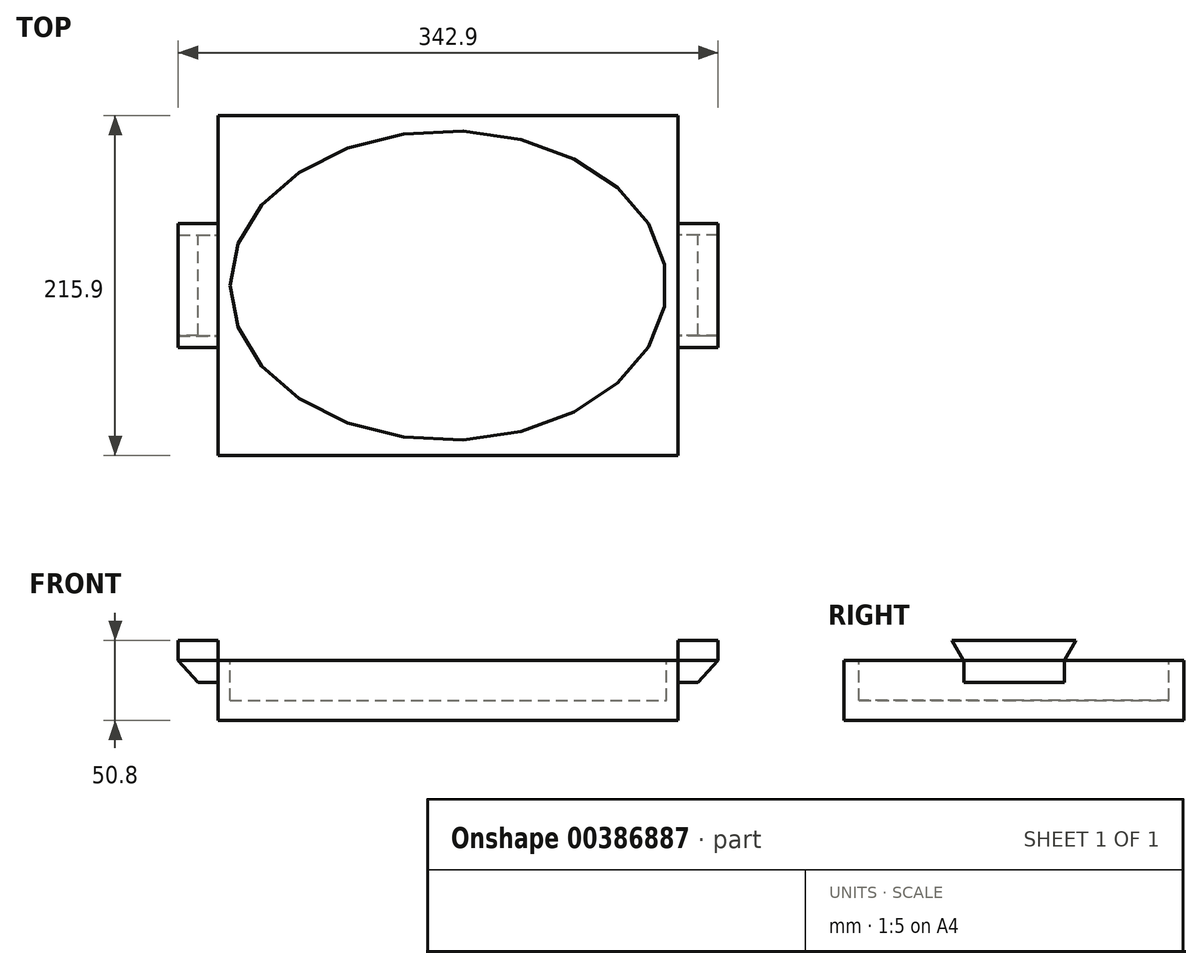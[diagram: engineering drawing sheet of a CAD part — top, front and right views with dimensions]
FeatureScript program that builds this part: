
annotation { "Feature Type Name" : "Feature", "Feature Type Description" : "" }
export const myFeature = defineFeature(function(context is Context, id is Id, definition is map)
    precondition{}
    {
        {
            var Q0;
            Q0=qCreatedBy(makeId("Top.planeOp"),FACE);
            var sketch = newSketch(context, id + "F0", { "sketchPlane" : qUnion([Q0])});
            skLineSegment(sketch, "E0.bottom", {"start": v(-146.05, 107.95) * mm, "end": v(146.05, 107.95) * mm});
            skLineSegment(sketch, "E0.top", {"start": v(-146.05, -107.95) * mm, "end": v(146.05, -107.95) * mm});
            skLineSegment(sketch, "E0.left", {"start": v(-146.05, 107.95) * mm, "end": v(-146.05, -107.95) * mm});
            skLineSegment(sketch, "E0.right", {"start": v(146.05, 107.95) * mm, "end": v(146.05, -107.95) * mm});
            skPoint(sketch, "E0.middle", {"position": v(0, 0) * mm});
            skSolve(sketch);
        }
        {
            var Q0;
            Q0=qSketchRegion(id+"F0",true);
            extrude(context, id + "F1", {"entities" : qUnion([Q0]), "depth" : 38.1 * mm});
        }
        {
            var Q0;
            Q0=makeQuery(id+"F1.opExtrude","CAP_FACE",FACE,{"disambiguationData":[OSD([sQuery(id+"F0.wireOp",EDGE,"E0.bottom"),sQuery(id+"F0.wireOp",EDGE,"E0.top"),sQuery(id+"F0.wireOp",EDGE,"E0.left"),sQuery(id+"F0.wireOp",EDGE,"E0.right")])],"isStart":false});
            var sketch = newSketch(context, id + "F2", { "sketchPlane" : qUnion([Q0])});
            skEllipse(sketch, "E1", {"center": v(0, 0) * mm, "majorRadius": 138.56 * mm, "minorRadius": 98.34 * mm, "majorAxis": v(-1, 0)});
            skSolve(sketch);
        }
        {
            var Q0;
            Q0=qSketchRegion(id+"F2",true);
            extrude(context, id + "F3", {"entities" : qUnion([Q0]), "operationType" : NewBodyOperationType.REMOVE, "oppositeDirection" : true, "depth" : 25.4 * mm});
        }
        {
            var Q0;
            Q0=makeQuery(id+"F1.opExtrude","SWEPT_FACE",FACE,{"disambiguationData":[OSD([sQuery(id+"F0.wireOp",EDGE,"E0.left")])]});
            var sketch = newSketch(context, id + "F4", { "sketchPlane" : qUnion([Q0])});
            skPoint(sketch, "E2.endSnap0", {"position": v(0, 38.1) * mm});
            skLineSegment(sketch, "E3", {"start": v(-32.14, 38.1) * mm, "end": v(-39.42, 50.8) * mm});
            skLineSegment(sketch, "E4", {"start": v(-39.42, 50.8) * mm, "end": v(39.42, 50.8) * mm});
            skLineSegment(sketch, "E5", {"start": v(32.14, 38.1) * mm, "end": v(39.42, 50.8) * mm});
            skLineSegment(sketch, "E6", {"start": v(-32.14, 38.1) * mm, "end": v(0, 38.1) * mm});
            skLineSegment(sketch, "E7", {"start": v(32.14, 38.1) * mm, "end": v(0, 38.1) * mm});
            skSolve(sketch);
        }
        {
            var Q0;
            Q0=qSketchRegion(id+"F4",true);
            extrude(context, id + "F5", {"entities" : qUnion([Q0]), "depth" : 25.4 * mm});
        }
        {
            var Q0;
            Q0=makeQuery(id+"F5.opExtrude","SWEPT_BODY",BODY,{"disambiguationData":[OSD([sQuery(id+"F4.wireOp",EDGE,"E3"),sQuery(id+"F4.wireOp",EDGE,"E4"),sQuery(id+"F4.wireOp",EDGE,"E5"),sQuery(id+"F4.wireOp",EDGE,"E6"),sQuery(id+"F4.wireOp",EDGE,"E7")])]});
            var Q1;
            Q1=qCreatedBy(makeId("Right.planeOp"),FACE);
            mirror(context, id + "F6", {"entities" : qUnion([Q0]), "mirrorPlane" : qUnion([Q1])});
        }
        {
            var Q0;
            Q0=makeQuery(id+"F1.opExtrude","SWEPT_FACE",FACE,{"disambiguationData":[OSD([sQuery(id+"F0.wireOp",EDGE,"E0.left")])]});
            var sketch = newSketch(context, id + "F7", { "sketchPlane" : qUnion([Q0])});
            skLineSegment(sketch, "E8", {"start": v(-32.07, 38.1) * mm, "end": v(31.8, 38.1) * mm});
            skLineSegment(sketch, "E9", {"start": v(31.8, 38.1) * mm, "end": v(31.8, 24) * mm});
            skLineSegment(sketch, "E10", {"start": v(31.8, 24) * mm, "end": v(-32.07, 24) * mm});
            skLineSegment(sketch, "E11", {"start": v(-32.07, 24) * mm, "end": v(-32.07, 38.1) * mm});
            skSolve(sketch);
        }
        {
            var Q0;
            Q0=qSketchRegion(id+"F7",true);
            extrude(context, id + "F8", {"entities" : qUnion([Q0]), "depth" : 25.4 * mm});
        }
        {
            var Q0;
            Q0=makeQuery(id+"F8.opExtrude","SWEPT_FACE",FACE,{"disambiguationData":[OSD([sQuery(id+"F7.wireOp",EDGE,"E11")])]});
            var sketch = newSketch(context, id + "F9", { "sketchPlane" : qUnion([Q0])});
            skLineSegment(sketch, "E12", {"start": v(171.45, 38.1) * mm, "end": v(158.75, 24) * mm});
            skLineSegment(sketch, "E13", {"start": v(158.75, 24) * mm, "end": v(171.45, 24) * mm});
            skLineSegment(sketch, "E14", {"start": v(171.45, 24) * mm, "end": v(171.45, 38.1) * mm});
            skSolve(sketch);
        }
        {
            var Q0;
            Q0=qSketchRegion(id+"F9",true);
            extrude(context, id + "F10", {"entities" : qUnion([Q0]), "operationType" : NewBodyOperationType.REMOVE, "oppositeDirection" : true, "depth" : 127 * mm});
        }
        {
            var Q0;
            Q0=makeQuery(id+"F8.opExtrude","SWEPT_BODY",BODY,{"disambiguationData":[OSD([sQuery(id+"F7.wireOp",EDGE,"E8"),sQuery(id+"F7.wireOp",EDGE,"E9"),sQuery(id+"F7.wireOp",EDGE,"E10"),sQuery(id+"F7.wireOp",EDGE,"E11")])]});
            var Q1;
            Q1=qCreatedBy(makeId("Right.planeOp"),FACE);
            mirror(context, id + "F11", {"entities" : qUnion([Q0]), "mirrorPlane" : qUnion([Q1])});
        }
    });
